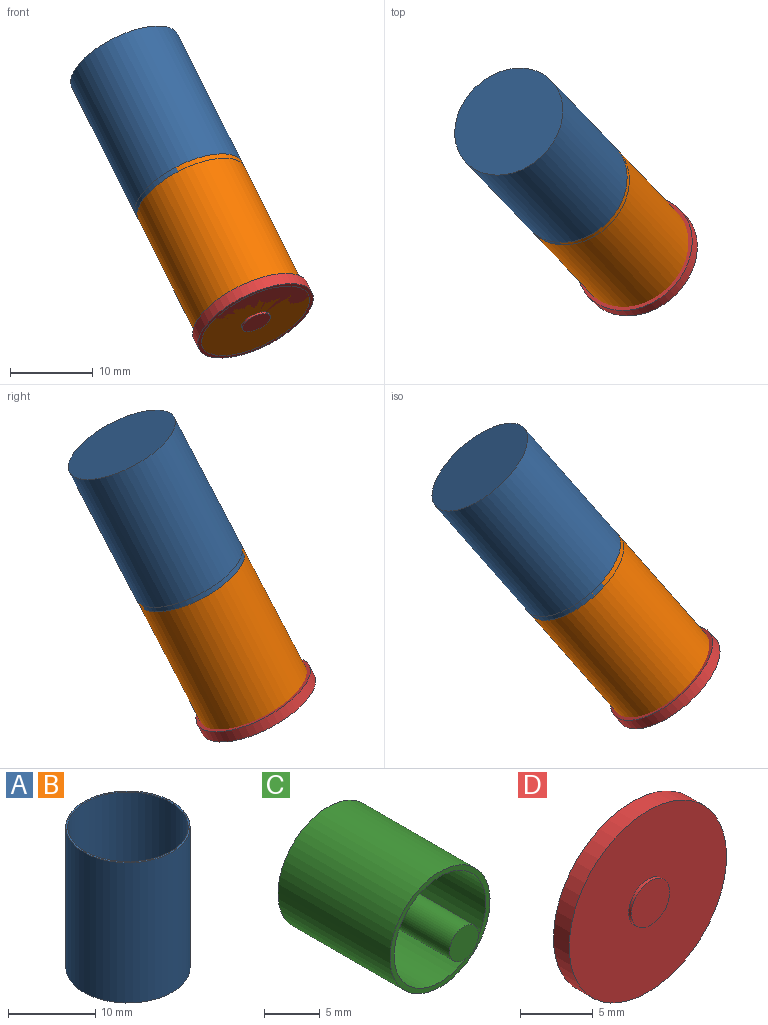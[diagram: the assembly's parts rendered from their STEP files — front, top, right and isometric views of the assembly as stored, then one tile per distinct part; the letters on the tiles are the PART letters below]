
ASSEMBLY  parts=4 mates=3
PART A: 5 faces, bbox 14.3x14.3x19.7 mm
  f0: plane 14.26x14.26mm, normal (0,0,-1), area 159.8mm2, adj f1
  f1: cylinder r=7.13mm len=19.71mm, axis (0,0,-1), area 883.3mm2, adj f0,f2
  f2: plane 14.26x14.26mm, normal (0,0,1), area 9.5mm2, adj f1,f3
  f3: cylinder r=6.92mm len=18.03mm, axis (0,0,1), area 783.9mm2, adj f2,f4
  f4: plane 13.84x13.84mm, normal (0,0,1), area 150.3mm2, adj f3
PART B: same geometry as A
PART C: 7 faces, bbox 12.7x17.3x12.7 mm
  f0: cylinder r=6.35mm len=14.22mm, axis (0,1,0), area 567.5mm2, adj f1,f2
  f1: plane 12.7x12.7mm, normal (0,-1,0), area 20.5mm2, adj f0,f3
  f2: plane 12.7x12.7mm, normal (0,1,0), area 126.7mm2, adj f0
  f3: cylinder r=5.81mm len=12.45mm, axis (0,-1,0), area 454.5mm2, adj f1,f4
  f4: plane 11.62x11.62mm, normal (0,-1,0), area 95.5mm2, adj f3,f5
  f5: cylinder r=1.84mm len=15.49mm, axis (0,1,0), area 178.9mm2, adj f4,f6
  f6: plane 3.68x3.68mm, normal (0,-1,0), area 10.6mm2, adj f5
PART D: 5 faces, bbox 15.2x1.8x15.2 mm
  f0: cylinder r=7.62mm len=15.24mm, axis (0,1,0), area 73mm2, adj f1,f2
  f1: plane 15.24x15.24mm, normal (0,-1,0), area 171.5mm2, adj f0,f3
  f2: plane 15.24x15.24mm, normal (0,1,0), area 182.4mm2, adj f0
  f3: cylinder r=1.87mm len=3.73mm, axis (0,1,0), area 3mm2, adj f1,f4
  f4: plane 3.73x3.73mm, normal (0,-1,0), area 10.9mm2, adj f3
PLACE A rot(axis=(0.57,0.82,-0.06),144.7deg) t=(-201.1,-26.07,-51.82)mm
PLACE B rot(axis=(-0.36,0.07,0.93),114.1deg) t=(-185.34,-42.54,-83.16)mm fixed
PLACE C rot(axis=(0.63,-0.75,-0.21),107deg) t=(-195.98,-31.42,-61.98)mm
PLACE D rot(axis=(0.65,-0.73,-0.19),103.8deg) t=(-185.95,-41.9,-81.93)mm
MATE slider B.f1 <-> A.f1  axis (0.41,-0.42,-0.81) through (-189.34,-38.36,-75.19)mm
MATE cylindrical C.f3 <-> B.f3  axis (0.41,-0.42,-0.81) through (-190.2,-37.46,-73.49)mm
MATE revolute B.f1 <-> D.f3  axis (0.41,-0.42,-0.81) through (-185.34,-42.54,-83.16)mm
